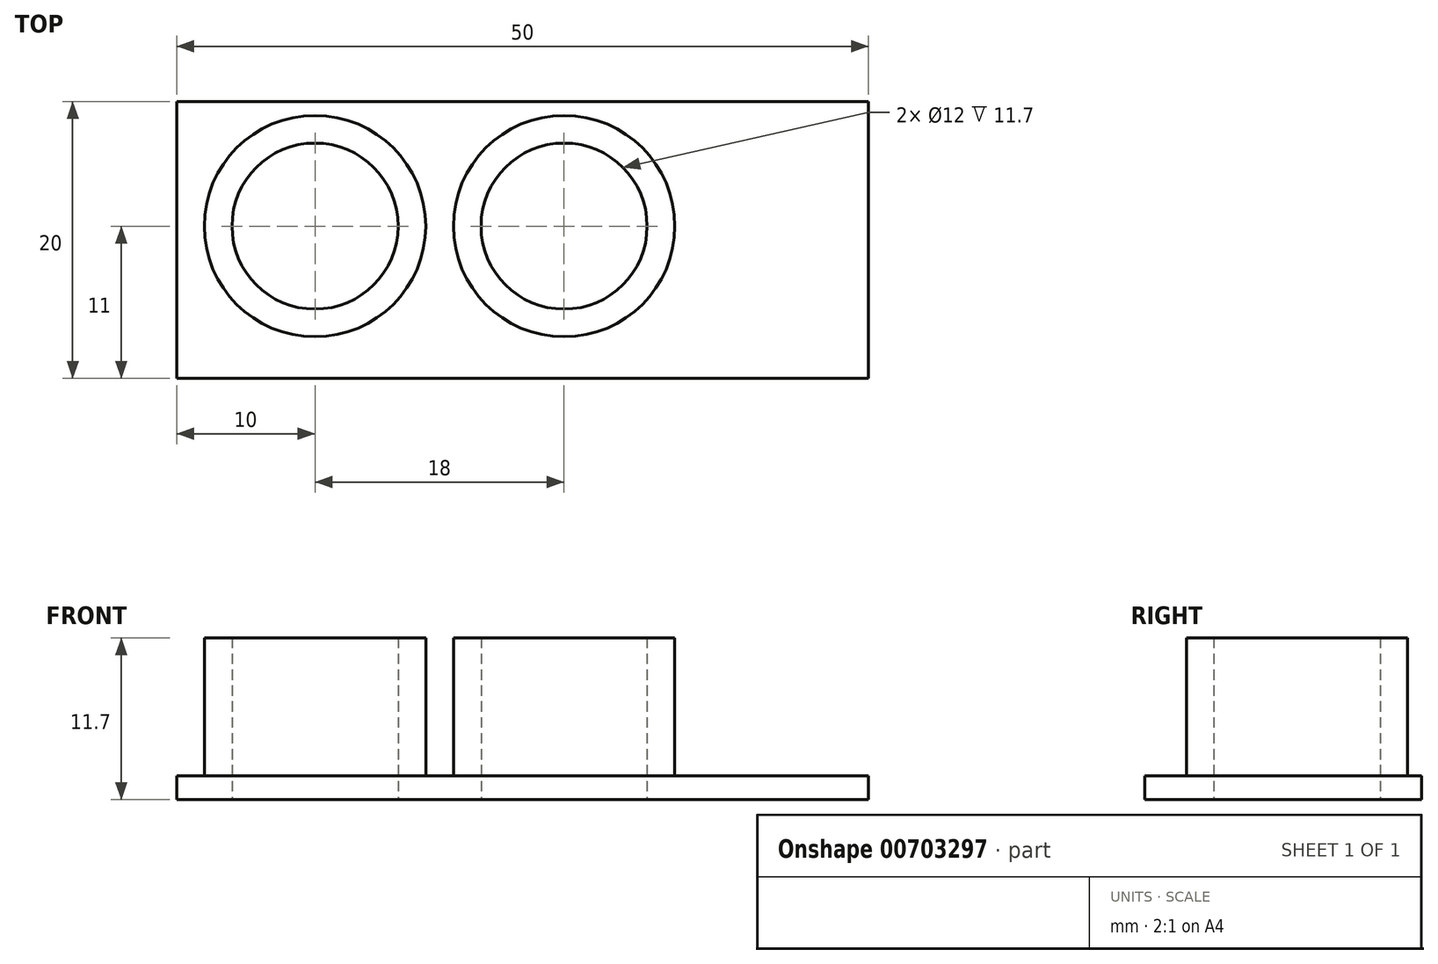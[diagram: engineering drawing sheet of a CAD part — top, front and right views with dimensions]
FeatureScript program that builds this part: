
annotation { "Feature Type Name" : "Feature", "Feature Type Description" : "" }
export const myFeature = defineFeature(function(context is Context, id is Id, definition is map)
    precondition{}
    {
        {
            var Q0;
            Q0=qCreatedBy(makeId("Top.planeOp"),FACE);
            var sketch = newSketch(context, id + "F0", { "sketchPlane" : qUnion([Q0])});
            skLineSegment(sketch, "E0.bottom", {"start": v(0, 0) * mm, "end": v(50, 0) * mm});
            skLineSegment(sketch, "E0.top", {"start": v(0, 20) * mm, "end": v(50, 20) * mm});
            skLineSegment(sketch, "E0.left", {"start": v(0, 0) * mm, "end": v(0, 20) * mm});
            skLineSegment(sketch, "E0.right", {"start": v(50, 0) * mm, "end": v(50, 20) * mm});
            skCircle(sketch, "E1", {"center": v(28, 11) * mm, "radius": 6 * mm});
            skCircle(sketch, "E2", {"center": v(10, 11) * mm, "radius": 6 * mm});
            skSolve(sketch);
        }
        {
            var Q0;
            Q0 = qSketchRegion(id + "F0", true);
            extrude(context, id + "F1", {"entities" : qUnion([Q0]), "depth" : 1.7 * mm, "offsetDistance" : 25 * mm});
        }
        {
            var Q0;
            Q0=makeQuery(id+"F1.opExtrude","CAP_FACE",FACE,{"disambiguationData":[OSD([sQuery(id+"F0.wireOp",EDGE,"E0.bottom"),sQuery(id+"F0.wireOp",EDGE,"E0.top"),sQuery(id+"F0.wireOp",EDGE,"E0.left"),sQuery(id+"F0.wireOp",EDGE,"E0.right"),sQuery(id+"F0.wireOp",EDGE,"E1"),sQuery(id+"F0.wireOp",EDGE,"E2")])],"isStart":false});
            var sketch = newSketch(context, id + "F2", { "sketchPlane" : qUnion([Q0])});
            skCircle(sketch, "E3", {"center": v(10, 11) * mm, "radius": 8 * mm});
            skCircle(sketch, "E4", {"center": v(28, 11) * mm, "radius": 8 * mm});
            skCircle(sketch, "E5", {"center": v(10, 11) * mm, "radius": 6 * mm});
            skPoint(sketch, "E5.first.point", {"position": v(12.19, 16.59) * mm});
            skPoint(sketch, "E5.second.point", {"position": v(15.4, 8.4) * mm});
            skPoint(sketch, "E5.third.point", {"position": v(4, 11) * mm});
            skPoint(sketch, "E6.first.point", {"position": v(25.51, 16.46) * mm});
            skPoint(sketch, "E6.second.point", {"position": v(25.51, 16.46) * mm});
            skPoint(sketch, "E6.third.point", {"position": v(33.5, 13.41) * mm});
            skSolve(sketch);
        }
        {
            var Q0;
            Q0=makeQuery(id+"F2.imprint","IMPRINT",FACE,{"disambiguationData":[TD([[makeQuery(id+"F2.imprint","IMPRINT",EDGE,{"derivedFrom":sQuery(id+"F2.wireOp",EDGE,"E3")}),1.0]])]});
            var Q1;
            Q1=makeQuery(id+"F2.imprint","IMPRINT",FACE,{"disambiguationData":[TD([[makeQuery(id+"F2.imprint","IMPRINT",EDGE,{"derivedFrom":sQuery(id+"F2.wireOp",EDGE,"E4")}),1.0]])]});
            extrude(context, id + "F3", {"entities" : qUnion([Q0, Q1]), "operationType" : NewBodyOperationType.ADD, "depth" : 10 * mm, "offsetDistance" : 25 * mm});
        }
        {
            var Q0;
            Q0=qCreatedBy(makeId("Right.planeOp"),FACE);
            cPlane(context, id + "F4", {"entities" : qUnion([Q0]), "cplaneType" : CPlaneType.OFFSET, "offset" : 10 * mm, "width" : 150 * mm, "height" : 150 * mm});
        }
    });
